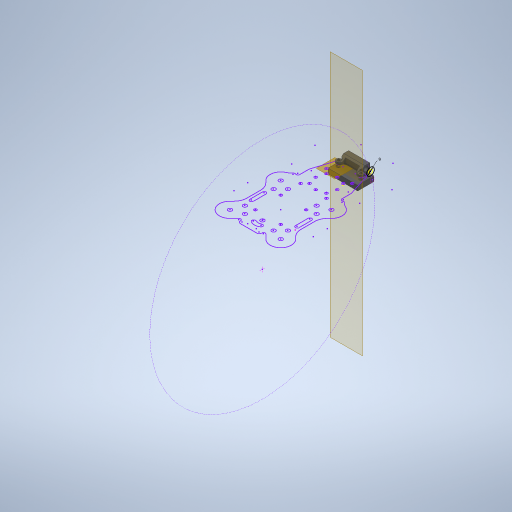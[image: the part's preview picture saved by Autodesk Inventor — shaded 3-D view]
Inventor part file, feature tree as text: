
AUTODESK INVENTOR PART (.ipt)
format: ipt  version: 2023 (Build 270158000, 158)  size: 866,304 bytes
history: native  units: in
note: dims shown in document units (in); Inventor stores cm internally (conversion verified against a paired STEP export)
features: sketch x22, extrude x18, projected_geometry x9, plane x7, fillet x2, chamfer x1
ambient origin geometry x8: Origin, YZ Plane, XZ Plane, XY Plane, X Axis, Y Axis, Z Axis, Center Point
bodies: Solid2 (feature_tree)
feature tree (59):
  plane  "Work Plane1"
  plane  "Work Plane7"
  plane  "Work Plane4"
  plane  "Work Plane9"
  sketch  "Sketch13"  dims[d22=0.1181in d23=0.0in d24=0.2008in]
  plane  "Work Plane11"
  extrude  "Extrusion10"  Depth=0.2008in
  plane  "Work Plane8"
  sketch  "Sketch15"  dims[d35=0.0001in d36=1.378in d37=0.0in]
  extrude  "Extrusion12"  Depth=1.378in TaperAngle=0.0deg
  extrude  "Extrusion13"  Depth=1.378in TaperAngle=0.0deg
  extrude  "Extrusion14"  Depth=0.2244in
  extrude  "Extrusion15"  Depth=1.378in TaperAngle=0.0deg
  sketch  "Sketch20"  dims[d47=0.1181in d48=0.1181in d49=0.0in]
  extrude  "Extrusion16"  Depth=0.1181in
  extrude  "Extrusion17"  Depth=0.1181in TaperAngle=0.0deg
  extrude  "Extrusion18"  Depth=0.0394in TaperAngle=0.0deg
  extrude  "Extrusion19"  Depth=0.0394in TaperAngle=0.0deg
  extrude  "Extrusion20"  Depth=0.1575in TaperAngle=0.0deg
  extrude  "Extrusion21"  Depth=0.0787in TaperAngle=0.0deg
  extrude  "Extrusion22"  [1 undecoded]
  extrude  "Extrusion23"  Depth=0.0787in
  extrude  "Extrusion24"  Depth=0.1378in TaperAngle=0.0deg
  extrude  "Extrusion25"  Depth=0.4921in
  plane  "Work Plane12"
  extrude  "Extrusion26"  Depth=0.0787in TaperAngle=45.0deg
  extrude  "Extrusion27"  Depth=0.3937in
  sketch  "Sketch32"  dims[d4=0.0197in]
  sketch  "Sketch33"  dims[d5=1.9685in]
  sketch  "Sketch35"  dims[d11=0.0197in]
  sketch  "Sketch36"  dims[d12=1.9685in d13=0.0197in d14=1.9685in d34=0.0197in d81=0.0197in]
  extrude  "Extrusion28"  Depth=1.9685in
  chamfer  "Chamfer1"  Distance=0.0197in
  fillet  "Fillet7"  Radius=1.9685in
  fillet  "Fillet8"  Radius=0.0197in
  sketch  "Sketch14"  dims[d25=0.2008in d32=1.378in d33=0.0in]
  sketch  "Sketch17"  dims[d38=0.0in d39=0.0in d40=0.2244in]
  sketch  "Sketch18"  dims[d41=0.2244in d42=1.378in d43=0.0in]
  projected_geometry  "Projected Loop7"
  projected_geometry  "Projected Loop8"
  sketch  "Sketch19"  dims[d44=0.1181in d45=0.0in d46=0.1181in]
  sketch  "Sketch21"  dims[d50=0.0394in d51=0.0in d52=0.0394in d53=0.0in]
  sketch  "Sketch22"  dims[d60=0.0118in d61=0.0394in d62=0.0in]
  projected_geometry  "Projected Loop9"
  sketch  "Sketch23"  dims[d63=0.1575in d64=0.0in d65=0.2963in d66=0.0in]
  projected_geometry  "Projected Loop10"
  projected_geometry  "Projected Loop11"
  sketch  "Sketch24"  dims[d67=0.0787in d68=0.0in d69=0.0787in d70=0.0in]
  sketch  "Sketch25"  dims[d71=0.3937in d72=0.0in d73=-3.0625in]
  projected_geometry  "Projected Loop12"
  sketch  "Sketch26"  dims[d74=0.0787in d75=0.0787in]
  projected_geometry  "Projected Loop13"
  sketch  "Sketch27"  dims[d76=0.2938in d77=0.0in d78=0.1378in d79=0.0in]
  projected_geometry  "Projected Loop14"
  sketch  "Sketch28"  dims[d82=0.3543in d83=0.4921in]
  projected_geometry  "Projected Loop15"
  sketch  "Sketch29"  dims[d84=0.1969in d85=0.0in d87=0.0197in d88=0.0787in d89=45.0deg]
  sketch  "Sketch30"  dims[d90=0.1969in d91=0.3937in]
  sketch  "Sketch31"  dims[d2=0.0197in d3=1.9685in]
note: 1 required parameter value undecoded (feature->parameter linkage not recoverable at this tier; creation-order binding heuristic only, values carry confidence <= 0.55)
